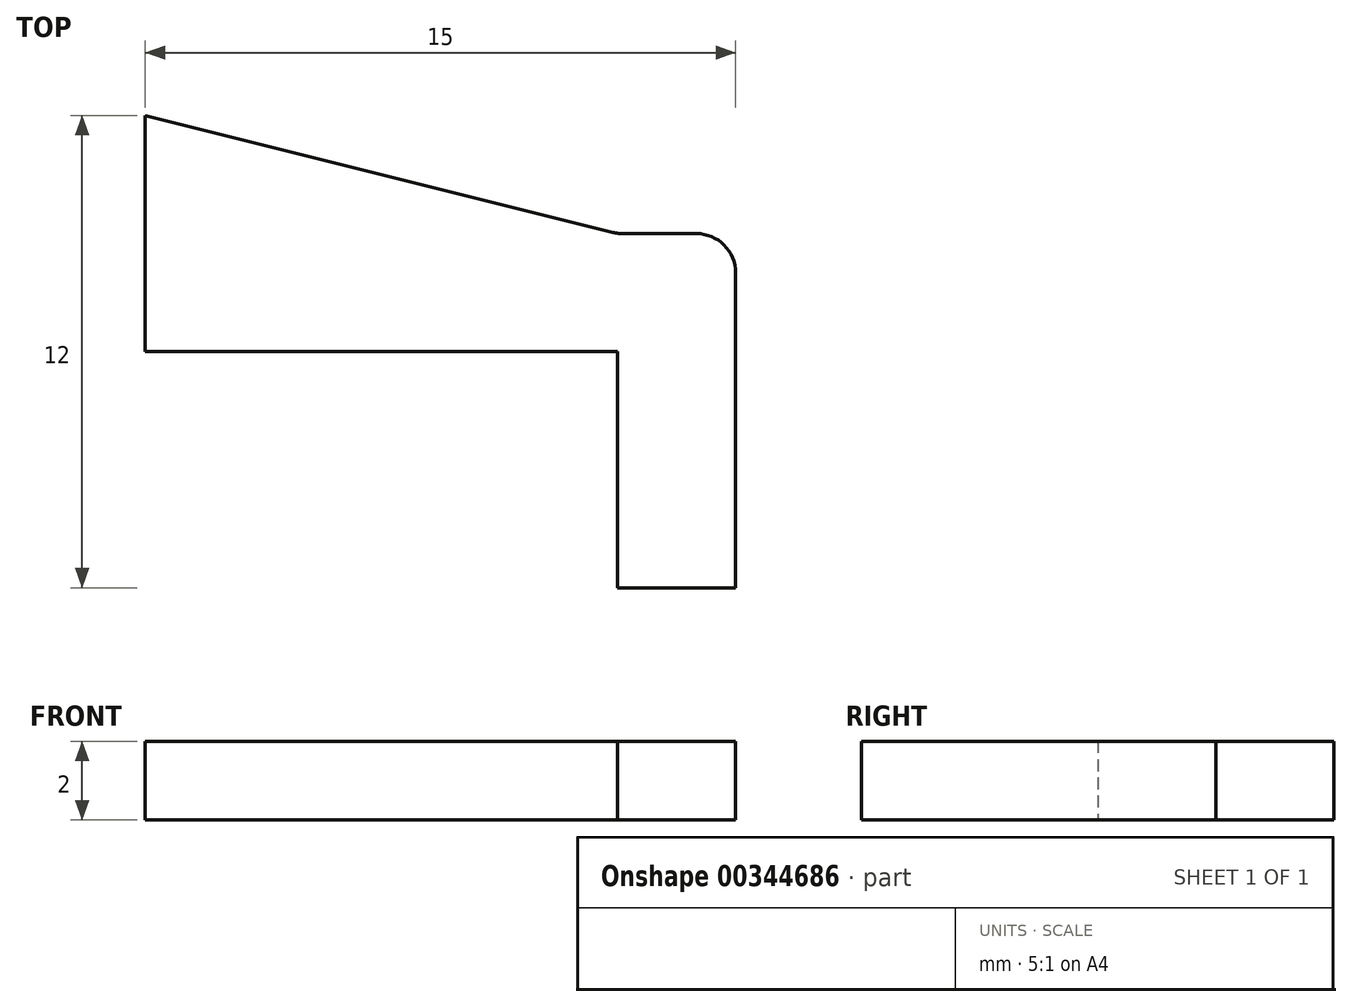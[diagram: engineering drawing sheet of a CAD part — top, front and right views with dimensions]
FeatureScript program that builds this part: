
annotation { "Feature Type Name" : "Feature", "Feature Type Description" : "" }
export const myFeature = defineFeature(function(context is Context, id is Id, definition is map)
    precondition{}
    {
        {
            var Q0;
            Q0=qCreatedBy(makeId("Top.planeOp"),FACE);
            var sketch = newSketch(context, id + "F0", { "sketchPlane" : qUnion([Q0])});
            skLineSegment(sketch, "E0", {"start": v(0, 0) * mm, "end": v(12, 0) * mm});
            skLineSegment(sketch, "E1", {"start": v(12, 0) * mm, "end": v(12, 3) * mm});
            skLineSegment(sketch, "E2", {"start": v(12, 3) * mm, "end": v(0, 6) * mm});
            skLineSegment(sketch, "E3", {"start": v(0, 6) * mm, "end": v(0, 3) * mm});
            skLineSegment(sketch, "E4", {"start": v(0, 3) * mm, "end": v(0, 3) * mm});
            skLineSegment(sketch, "E5", {"start": v(0, 3) * mm, "end": v(0, 0) * mm});
            skSolve(sketch);
        }
        {
            var Q0;
            Q0=makeQuery(id+"F0.imprint","IMPRINT",FACE,{"disambiguationData":[TD([[makeQuery(id+"F0.imprint","IMPRINT",EDGE,{"derivedFrom":sQuery(id+"F0.wireOp",EDGE,"E0")}),1.0]])]});
            extrude(context, id + "F1", {"entities" : qUnion([Q0]), "depth" : 2 * mm});
        }
        {
            var Q0;
            Q0=makeQuery(id+"F1.opExtrude","CAP_FACE",FACE,{"disambiguationData":[OSD([sQuery(id+"F0.wireOp",EDGE,"E0"),sQuery(id+"F0.wireOp",EDGE,"E1"),sQuery(id+"F0.wireOp",EDGE,"E2"),sQuery(id+"F0.wireOp",EDGE,"E3"),sQuery(id+"F0.wireOp",EDGE,"E5")])],"isStart":false});
            var sketch = newSketch(context, id + "F2", { "sketchPlane" : qUnion([Q0])});
            skLineSegment(sketch, "E6", {"start": v(12, 3) * mm, "end": v(15, 3) * mm});
            skLineSegment(sketch, "E7", {"start": v(15, 3) * mm, "end": v(15, -6) * mm});
            skLineSegment(sketch, "E8", {"start": v(15, -6) * mm, "end": v(12, -6) * mm});
            skLineSegment(sketch, "E9", {"start": v(12, -6) * mm, "end": v(12, 0) * mm});
            skSolve(sketch);
        }
        {
            var Q0;
            Q0=makeQuery(id+"F2.imprint","IMPRINT",FACE,{"disambiguationData":[TD([[makeQuery(id+"F2.imprint","IMPRINT",EDGE,{"derivedFrom":sQuery(id+"F2.wireOp",EDGE,"E6")}),-1.0]])]});
            var Q1;
            Q1=makeQuery(id+"F1.opExtrude","CAP_FACE",FACE,{"disambiguationData":[OSD([sQuery(id+"F0.wireOp",EDGE,"E0"),sQuery(id+"F0.wireOp",EDGE,"E1"),sQuery(id+"F0.wireOp",EDGE,"E2"),sQuery(id+"F0.wireOp",EDGE,"E3"),sQuery(id+"F0.wireOp",EDGE,"E5")])],"isStart":true});
            extrude(context, id + "F3", {"entities" : qUnion([Q0]), "operationType" : NewBodyOperationType.ADD, "endBound" : BoundingType.UP_TO_SURFACE, "oppositeDirection" : true, "endBoundEntityFace" : qUnion([Q1]), "depth" : 25 * mm});
        }
        {
            var Q0;
            Q0=makeQuery(id+"F1.opExtrude","SWEPT_EDGE",EDGE,{"disambiguationData":[OSD([sQuery(id+"F0.wireOp",EDGE,"E0"),sQuery(id+"F0.wireOp",EDGE,"E1")])]});
            var Q1;
            {var subQ0=sQuery(id+"F0.wireOp",EDGE,"E2");var subQ1=sQuery(id+"F0.wireOp",EDGE,"E1");Q1=makeQuery(id+"F3.boolean.opBoolean","MERGE",EDGE,{"derivedFrom":[makeQuery(id+"F1.opExtrude","SWEPT_EDGE",EDGE,{"disambiguationData":[OSD([subQ1,subQ0])]}),makeQuery(id+"F3.opExtrude","SWEPT_EDGE",EDGE,{"disambiguationData":[OSD([subQ1,subQ0,sQuery(id+"F2.wireOp",EDGE,"E6")])]})]});}
            var Q2;
            Q2=makeQuery(id+"F3.opExtrude","SWEPT_EDGE",EDGE,{"disambiguationData":[OSD([sQuery(id+"F2.wireOp",EDGE,"E6"),sQuery(id+"F2.wireOp",EDGE,"E7")])]});
            fillet(context, id + "F4", {"entities" : qUnion([Q0, Q1, Q2]), "radius" : 1 * mm, "tangentPropagation" : true, "allowEdgeOverflow" : false});
        }
    });
